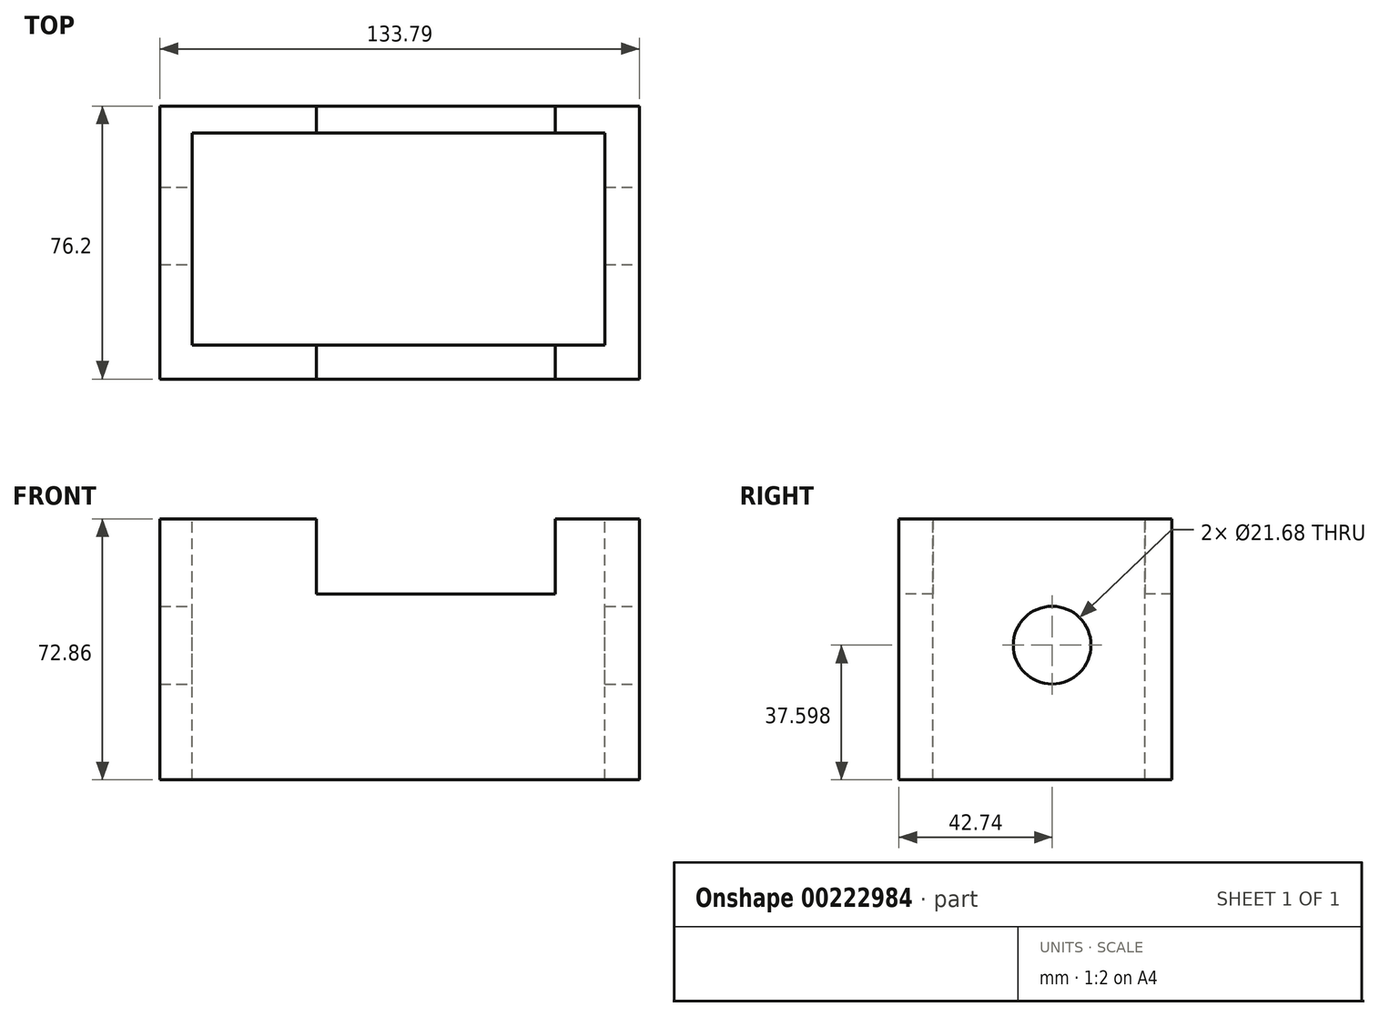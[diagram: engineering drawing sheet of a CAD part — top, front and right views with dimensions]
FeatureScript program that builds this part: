
annotation { "Feature Type Name" : "Feature", "Feature Type Description" : "" }
export const myFeature = defineFeature(function(context is Context, id is Id, definition is map)
    precondition{}
    {
        {
            var Q0;
            Q0=qCreatedBy(makeId("Front.planeOp"),FACE);
            var sketch = newSketch(context, id + "F0", { "sketchPlane" : qUnion([Q0])});
            skLineSegment(sketch, "E0.bottom", {"start": v(-99.66, 21.05) * mm, "end": v(34.13, 21.05) * mm});
            skLineSegment(sketch, "E0.top", {"start": v(-99.66, -51.81) * mm, "end": v(34.13, -51.81) * mm});
            skLineSegment(sketch, "E0.left", {"start": v(-99.66, 21.05) * mm, "end": v(-99.66, -51.81) * mm});
            skLineSegment(sketch, "E0.right", {"start": v(34.13, 21.05) * mm, "end": v(34.13, -51.81) * mm});
            skSolve(sketch);
        }
        {
            var Q0;
            Q0 = qSketchRegion(id + "F0", true);
            extrude(context, id + "F1", {"entities" : qUnion([Q0]), "oppositeDirection" : true, "depth" : 76.2 * mm});
        }
        {
            var Q0;
            Q0=makeQuery(id+"F1.opExtrude","SWEPT_FACE",FACE,{"disambiguationData":[OSD([sQuery(id+"F0.wireOp",EDGE,"E0.bottom")])]});
            var sketch = newSketch(context, id + "F2", { "sketchPlane" : qUnion([Q0])});
            skLineSegment(sketch, "E1.bottom", {"start": v(-90.7, 9.42) * mm, "end": v(24.55, 9.42) * mm});
            skLineSegment(sketch, "E1.top", {"start": v(-90.7, 68.66) * mm, "end": v(24.55, 68.66) * mm});
            skLineSegment(sketch, "E1.left", {"start": v(-90.7, 9.42) * mm, "end": v(-90.7, 68.66) * mm});
            skLineSegment(sketch, "E1.right", {"start": v(24.55, 9.42) * mm, "end": v(24.55, 68.66) * mm});
            skSolve(sketch);
        }
        {
            var Q0;
            Q0 = qSketchRegion(id + "F2", true);
            extrude(context, id + "F3", {"entities" : qUnion([Q0]), "operationType" : NewBodyOperationType.REMOVE, "endBound" : BoundingType.THROUGH_ALL, "oppositeDirection" : true, "depth" : 76.2 * mm});
        }
        {
            var Q0;
            Q0=makeQuery(id+"F1.opExtrude","SWEPT_FACE",FACE,{"disambiguationData":[OSD([sQuery(id+"F0.wireOp",EDGE,"E0.right")])]});
            var sketch = newSketch(context, id + "F4", { "sketchPlane" : qUnion([Q0])});
            skCircle(sketch, "E2", {"center": v(42.74, -14.21) * mm, "radius": 10.84 * mm});
            skSolve(sketch);
        }
        {
            var Q0;
            Q0 = qSketchRegion(id + "F4", true);
            extrude(context, id + "F5", {"entities" : qUnion([Q0]), "operationType" : NewBodyOperationType.REMOVE, "endBound" : BoundingType.THROUGH_ALL, "oppositeDirection" : true, "depth" : 25.4 * mm});
        }
        {
            var Q0;
            Q0=makeQuery(id+"F1.opExtrude","CAP_FACE",FACE,{"disambiguationData":[OSD([sQuery(id+"F0.wireOp",EDGE,"E0.bottom"),sQuery(id+"F0.wireOp",EDGE,"E0.top"),sQuery(id+"F0.wireOp",EDGE,"E0.left"),sQuery(id+"F0.wireOp",EDGE,"E0.right")])],"isStart":true});
            var sketch = newSketch(context, id + "F6", { "sketchPlane" : qUnion([Q0])});
            skLineSegment(sketch, "E3.bottom", {"start": v(-56.04, 33.35) * mm, "end": v(10.68, 33.35) * mm});
            skLineSegment(sketch, "E3.top", {"start": v(-56.04, 0) * mm, "end": v(10.68, 0) * mm});
            skLineSegment(sketch, "E3.left", {"start": v(-56.04, 33.35) * mm, "end": v(-56.04, 0) * mm});
            skLineSegment(sketch, "E3.right", {"start": v(10.68, 33.35) * mm, "end": v(10.68, 0) * mm});
            skSolve(sketch);
        }
        {
            var Q0;
            Q0 = qSketchRegion(id + "F6", true);
            extrude(context, id + "F7", {"entities" : qUnion([Q0]), "operationType" : NewBodyOperationType.REMOVE, "endBound" : BoundingType.THROUGH_ALL, "oppositeDirection" : true, "depth" : 76.2 * mm});
        }
    });
